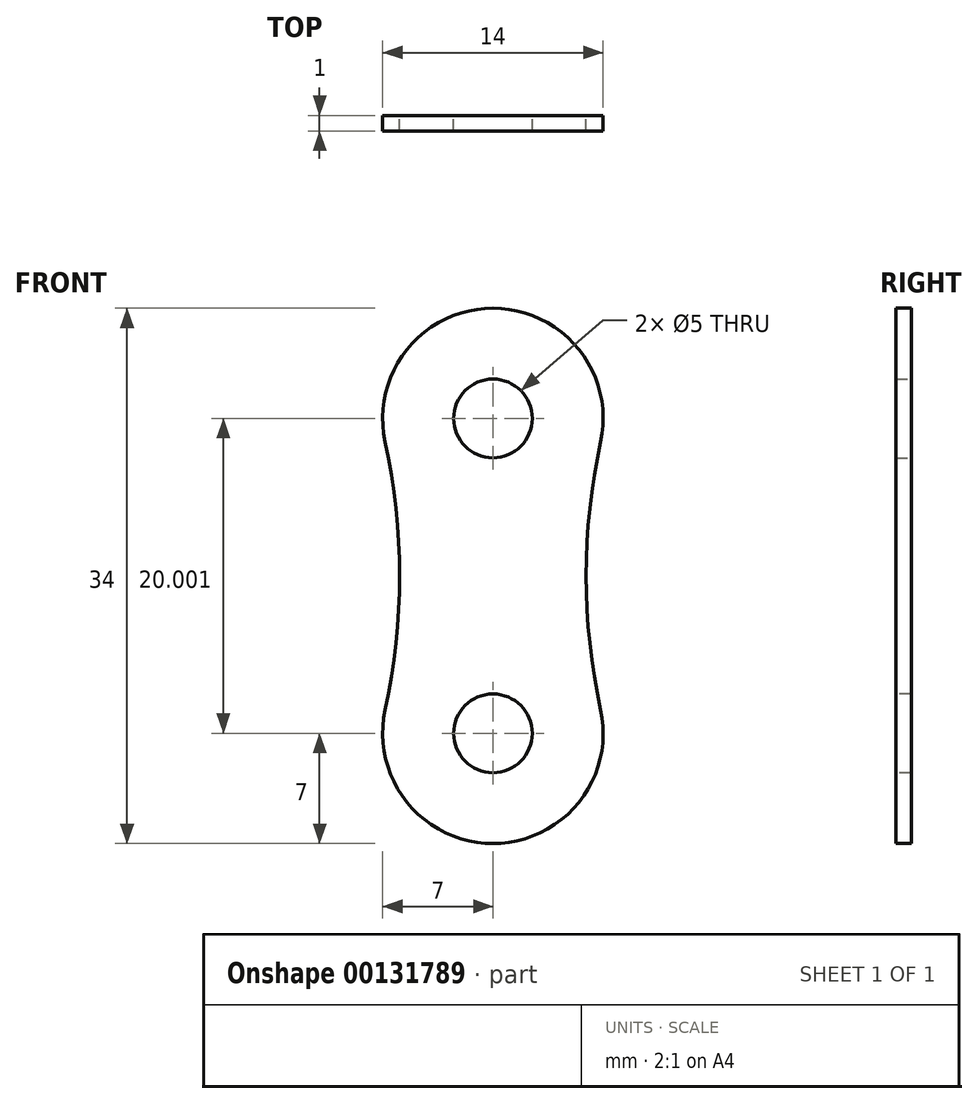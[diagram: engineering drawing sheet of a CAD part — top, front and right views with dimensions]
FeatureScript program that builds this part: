
annotation { "Feature Type Name" : "Feature", "Feature Type Description" : "" }
export const myFeature = defineFeature(function(context is Context, id is Id, definition is map)
    precondition{}
    {
        {
            var Q0;
            Q0=qCreatedBy(makeId("Front.planeOp"),FACE);
            var sketch = newSketch(context, id + "F0", { "sketchPlane" : qUnion([Q0])});
            skArc(sketch, "E0", {"start": v(-6.84, 1.49) * mm, "mid": v(0, -7) * mm, "end": v(6.84, 1.49) * mm});
            skArc(sketch, "E1", {"start": v(6.84, 18.51) * mm, "mid": v(5.92, 10) * mm, "end": v(6.84, 1.49) * mm});
            skArc(sketch, "E2.MirrorC", {"start": v(-6.84, 18.51) * mm, "mid": v(-5.92, 10) * mm, "end": v(-6.84, 1.49) * mm});
            skArc(sketch, "E3", {"start": v(6.84, 18.51) * mm, "mid": v(0, 27) * mm, "end": v(-6.84, 18.51) * mm});
            skCircle(sketch, "E4", {"center": v(0, 20) * mm, "radius": 2.5 * mm});
            skSolve(sketch);
        }
        {
            var Q0;
            Q0=makeQuery(id+"F0.imprint","IMPRINT",FACE,{"disambiguationData":[TD([[makeQuery(id+"F0.imprint","IMPRINT",EDGE,{"derivedFrom":sQuery(id+"F0.wireOp",EDGE,"E0")}),1.0]])]});
            extrude(context, id + "F1", {"entities" : qUnion([Q0]), "depth" : 1 * mm});
        }
        {
            var Q0;
            Q0=makeQuery(id+"F1.opExtrude","CAP_FACE",FACE,{"disambiguationData":[OSD([sQuery(id+"F0.wireOp",EDGE,"E0"),sQuery(id+"F0.wireOp",EDGE,"E1"),sQuery(id+"F0.wireOp",EDGE,"E2.MirrorC"),sQuery(id+"F0.wireOp",EDGE,"E3"),sQuery(id+"F0.wireOp",EDGE,"E4")])],"isStart":false});
            var sketch = newSketch(context, id + "F2", { "sketchPlane" : qUnion([Q0])});
            skCircle(sketch, "E5", {"center": v(0, 0) * mm, "radius": 2.5 * mm});
            skSolve(sketch);
        }
        {
            var Q0;
            Q0 = qSketchRegion(id + "F2", true);
            extrude(context, id + "F3", {"entities" : qUnion([Q0]), "operationType" : NewBodyOperationType.REMOVE, "oppositeDirection" : true, "depth" : 1 * mm});
        }
    });
